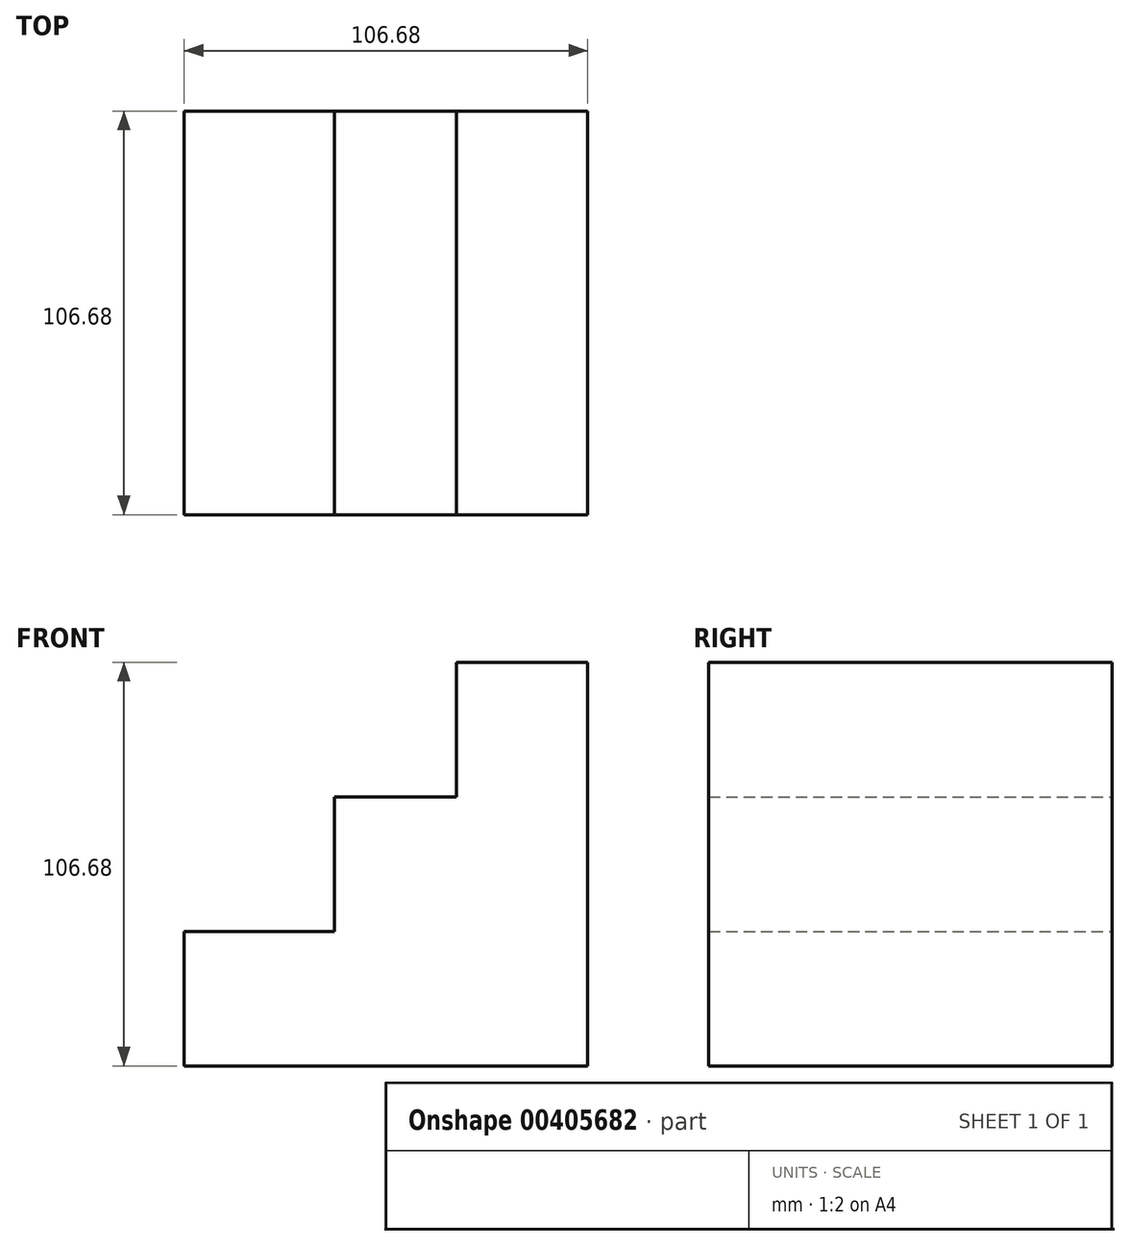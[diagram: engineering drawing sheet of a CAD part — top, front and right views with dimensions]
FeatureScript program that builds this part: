
annotation { "Feature Type Name" : "Feature", "Feature Type Description" : "" }
export const myFeature = defineFeature(function(context is Context, id is Id, definition is map)
    precondition{}
    {
        {
            var Q0;
            Q0=qCreatedBy(makeId("Front.planeOp"),FACE);
            var sketch = newSketch(context, id + "F0", { "sketchPlane" : qUnion([Q0])});
            skLineSegment(sketch, "E0.bottom", {"start": v(-53.34, 53.34) * mm, "end": v(53.34, 53.34) * mm});
            skLineSegment(sketch, "E0.top", {"start": v(-53.34, -53.34) * mm, "end": v(53.34, -53.34) * mm});
            skLineSegment(sketch, "E0.left", {"start": v(-53.34, 53.34) * mm, "end": v(-53.34, -53.34) * mm});
            skLineSegment(sketch, "E0.right", {"start": v(53.34, 53.34) * mm, "end": v(53.34, -53.34) * mm});
            skPoint(sketch, "E0.middle", {"position": v(0, 0) * mm});
            skLineSegment(sketch, "E1", {"start": v(53.34, 53.34) * mm, "end": v(18.6, 53.34) * mm});
            skLineSegment(sketch, "E2", {"start": v(18.6, 53.34) * mm, "end": v(18.6, 17.78) * mm});
            skLineSegment(sketch, "E3", {"start": v(18.6, 17.78) * mm, "end": v(-13.7, 17.78) * mm});
            skLineSegment(sketch, "E4", {"start": v(-13.7, 17.78) * mm, "end": v(-13.7, -17.78) * mm});
            skLineSegment(sketch, "E5", {"start": v(-13.7, -17.78) * mm, "end": v(-53.34, -17.78) * mm});
            skSolve(sketch);
        }
        {
            var Q0;
            {var subQ1=sQuery(id+"F0.wireOp",EDGE,"E0.top");Q0=makeQuery(id+"F0.imprint","IMPRINT",FACE,{"disambiguationData":[TD([[makeQuery(id+"F0.imprint","IMPRINT",EDGE,{"derivedFrom":subQ1}),1.0]])]});}
            extrude(context, id + "F1", {"entities" : qUnion([Q0]), "depth" : 106.68 * mm});
        }
    });
